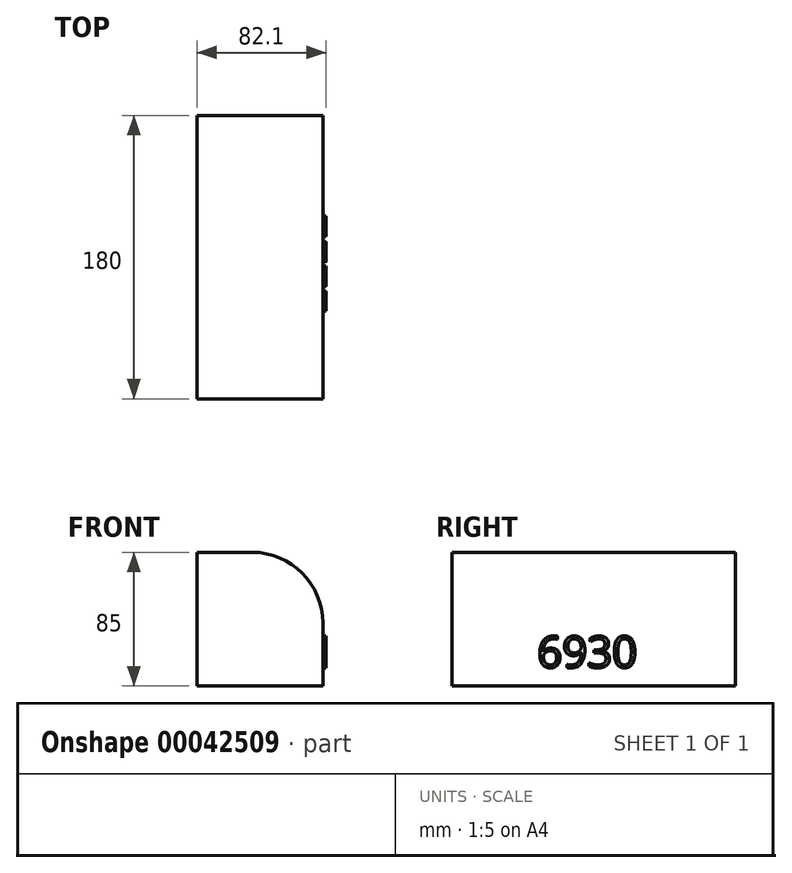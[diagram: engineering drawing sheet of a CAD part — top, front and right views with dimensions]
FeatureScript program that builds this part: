
annotation { "Feature Type Name" : "Feature", "Feature Type Description" : "" }
export const myFeature = defineFeature(function(context is Context, id is Id, definition is map)
    precondition{}
    {
        {
            var Q0;
            Q0=qCreatedBy(makeId("Front.planeOp"),FACE);
            var sketch = newSketch(context, id + "F0", { "sketchPlane" : qUnion([Q0])});
            skLineSegment(sketch, "E0.bottom", {"start": v(-54.88, 12.2) * mm, "end": v(25.12, 12.2) * mm});
            skLineSegment(sketch, "E0.top", {"start": v(-54.88, -72.8) * mm, "end": v(25.12, -72.8) * mm});
            skLineSegment(sketch, "E0.left", {"start": v(-54.88, 12.2) * mm, "end": v(-54.88, -72.8) * mm});
            skLineSegment(sketch, "E0.right", {"start": v(25.12, 12.2) * mm, "end": v(25.12, -72.8) * mm});
            skSolve(sketch);
        }
        {
            var Q0;
            Q0=makeQuery(id+"F0.imprint","IMPRINT",FACE,{"disambiguationData":[TD([[makeQuery(id+"F0.imprint","IMPRINT",EDGE,{"derivedFrom":sQuery(id+"F0.wireOp",EDGE,"E0.bottom")}),-1.0]])]});
            extrude(context, id + "F1", {"entities" : qUnion([Q0]), "depth" : 180 * mm});
        }
        {
            var Q0;
            Q0=makeQuery(id+"F1.opExtrude","SWEPT_EDGE",EDGE,{"disambiguationData":[OSD([sQuery(id+"F0.wireOp",EDGE,"E0.bottom"),sQuery(id+"F0.wireOp",EDGE,"E0.right")])]});
            fillet(context, id + "F2", {"entities" : qUnion([Q0]), "radius" : 44.95 * mm, "tangentPropagation" : true, "allowEdgeOverflow" : false});
        }
        {
            var Q0;
            Q0=makeQuery(id+"F1.opExtrude","SWEPT_FACE",FACE,{"disambiguationData":[OSD([sQuery(id+"F0.wireOp",EDGE,"E0.right")])]});
            var sketch = newSketch(context, id + "F3", { "sketchPlane" : qUnion([Q0])});
            skText(sketch, "E1", { "text": "6930\n", "fontName": "OpenSans-Regular.ttf"});
            const initialGuessF3  = {"E1": [-0.1259, -0.06099, 1, 0, 0.01995]};
            skSetInitialGuess(sketch, initialGuessF3);
            skSolve(sketch);
        }
        {
            var Q0;
            Q0 = qSketchRegion(id + "F3", true);
            extrude(context, id + "F4", {"entities" : qUnion([Q0]), "operationType" : NewBodyOperationType.ADD, "depth" : 2.1 * mm});
        }
    });
